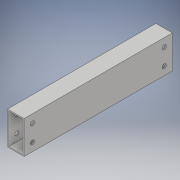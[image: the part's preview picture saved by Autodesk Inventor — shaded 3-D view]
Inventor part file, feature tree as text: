
AUTODESK INVENTOR PART (.ipt)
format: ipt  version: 2018 (Build 220112000, 112)  size: 115,200 bytes
history: native  units: in
note: dims shown in document units (in); Inventor stores cm internally (conversion verified against a paired STEP export)
features: hole x4, extrude x1, shell x1, sketch x1
ambient origin geometry x8: Origin, YZ Plane, XZ Plane, XY Plane, X Axis, Y Axis, Z Axis, Center Point
bodies: Solid1 (feature_tree)
feature tree (7):
  extrude  "Extrusion1"  Depth=2.0in
  shell  "Shell1"  Thickness=9.0in
  hole  "Hole1"  [1 undecoded]
  hole  "Hole2"  [1 undecoded]
  hole  "Hole3"  [1 undecoded]
  hole  "Hole4"  [1 undecoded]
  sketch  "Sketch1"  dims[d0=1.0in d1=2.0in d2=9.0in d3=0.0in d4=0.0625in d5=0.5in d6=0.5in d7=0.25in d8=0.75in d9=0.375in d10=0.25in d11=0.5635in d12=1.0in d13=0.8108in d14=0.5in d15=0.5in d16=0.25in d17=0.75in d18=0.375in d19=0.25in d20=0.5635in d21=1.0in d22=0.8108in d23=0.5in d24=0.5in d25=0.25in d26=0.75in d27=0.375in d28=0.25in d29=0.5635in d30=1.0in d31=0.8108in d32=0.5in d33=0.5in d34=0.25in d35=0.75in d36=0.375in d37=0.25in d38=0.5635in d39=1.0in d40=0.8108in]
note: 4 required parameter values undecoded (feature->parameter linkage not recoverable at this tier; creation-order binding heuristic only, values carry confidence <= 0.55)
